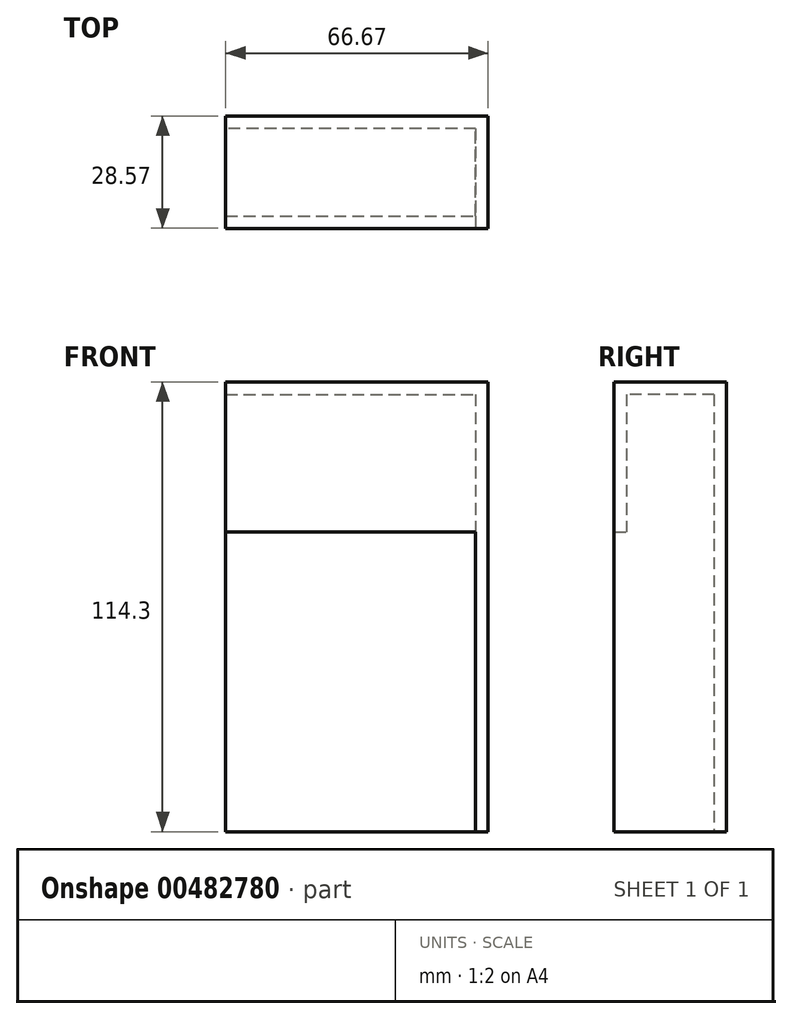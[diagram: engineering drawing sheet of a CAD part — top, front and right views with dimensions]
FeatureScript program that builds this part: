
annotation { "Feature Type Name" : "Feature", "Feature Type Description" : "" }
export const myFeature = defineFeature(function(context is Context, id is Id, definition is map)
    precondition{}
    {
        {
            var Q0;
            Q0=qCreatedBy(makeId("Front.planeOp"),FACE);
            var sketch = newSketch(context, id + "F0", { "sketchPlane" : qUnion([Q0])});
            skLineSegment(sketch, "E0.bottom", {"start": v(-31.75, 19.05) * mm, "end": v(31.75, 19.05) * mm});
            skLineSegment(sketch, "E0.top", {"start": v(-31.75, -19.05) * mm, "end": v(31.75, -19.05) * mm});
            skLineSegment(sketch, "E0.left", {"start": v(-31.75, 19.05) * mm, "end": v(-31.75, -19.05) * mm});
            skLineSegment(sketch, "E0.right", {"start": v(31.75, 19.05) * mm, "end": v(31.75, -19.05) * mm});
            skPoint(sketch, "E1", {"position": v(0, 0) * mm});
            skPoint(sketch, "E1.positionSnap0", {"position": v(-31.75, 0) * mm});
            skPoint(sketch, "E1.positionSnap1", {"position": v(0, 19.05) * mm});
            skSolve(sketch);
        }
        {
            var Q0;
            Q0=makeQuery(id+"F0.imprint","IMPRINT",FACE,{"disambiguationData":[TD([[makeQuery(id+"F0.imprint","IMPRINT",EDGE,{"derivedFrom":sQuery(id+"F0.wireOp",EDGE,"E0.bottom")}),-1.0]])]});
            extrude(context, id + "F1", {"entities" : qUnion([Q0]), "depth" : 3.17 * mm});
        }
        {
            var Q0;
            Q0=makeQuery(id+"F1.opExtrude","SWEPT_FACE",FACE,{"disambiguationData":[OSD([sQuery(id+"F0.wireOp",EDGE,"E0.right")])]});
            var sketch = newSketch(context, id + "F2", { "sketchPlane" : qUnion([Q0])});
            skLineSegment(sketch, "E2.bottom", {"start": v(-3.18, 19.05) * mm, "end": v(22.23, 19.05) * mm});
            skLineSegment(sketch, "E2.top", {"start": v(-3.18, -19.05) * mm, "end": v(22.23, -19.05) * mm});
            skLineSegment(sketch, "E2.left", {"start": v(-3.18, 19.05) * mm, "end": v(-3.18, -19.05) * mm});
            skLineSegment(sketch, "E2.right", {"start": v(22.23, 19.05) * mm, "end": v(22.23, -19.05) * mm});
            skSolve(sketch);
        }
        {
            var Q0;
            {var subQ2=sQuery(id+"F2.wireOp",EDGE,"E2.right");Q0=makeQuery(id+"F2.imprint","IMPRINT",FACE,{"disambiguationData":[TD([[makeQuery(id+"F2.imprint","IMPRINT",EDGE,{"derivedFrom":subQ2}),-1.0]])]});}
            var Q1;
            {var subQ2=sQuery(id+"F2.wireOp",EDGE,"E2.left");Q1=makeQuery(id+"F2.imprint","IMPRINT",FACE,{"disambiguationData":[TD([[makeQuery(id+"F2.imprint","IMPRINT",EDGE,{"derivedFrom":subQ2}),1.0]])]});}
            extrude(context, id + "F3", {"entities" : qUnion([Q0, Q1]), "operationType" : NewBodyOperationType.ADD, "depth" : 3.17 * mm});
        }
        {
            var Q0;
            Q0=makeQuery(id+"F3.boolean.opBoolean","MERGE",FACE,{"derivedFrom":[makeQuery(id+"F1.opExtrude","SWEPT_FACE",FACE,{"disambiguationData":[OSD([sQuery(id+"F0.wireOp",EDGE,"E0.top")])]}),makeQuery(id+"F3.opExtrude","SWEPT_FACE",FACE,{"disambiguationData":[OSD([sQuery(id+"F2.wireOp",EDGE,"E2.top")])]})]});
            var sketch = newSketch(context, id + "F4", { "sketchPlane" : qUnion([Q0])});
            skLineSegment(sketch, "E3.bottom", {"start": v(34.92, -22.23) * mm, "end": v(31.75, -22.23) * mm});
            skLineSegment(sketch, "E3.top", {"start": v(34.92, 3.18) * mm, "end": v(31.75, 3.18) * mm});
            skLineSegment(sketch, "E3.left", {"start": v(34.92, -22.23) * mm, "end": v(34.92, 3.18) * mm});
            skLineSegment(sketch, "E3.right", {"start": v(31.75, -22.23) * mm, "end": v(31.75, 3.18) * mm});
            skSolve(sketch);
        }
        {
            var Q0;
            {var subQ1=sQuery(id+"F4.wireOp",EDGE,"E3.bottom");Q0=makeQuery(id+"F4.imprint","IMPRINT",FACE,{"disambiguationData":[TD([[makeQuery(id+"F4.imprint","IMPRINT",EDGE,{"derivedFrom":subQ1}),-1.0]])]});}
            extrude(context, id + "F5", {"entities" : qUnion([Q0]), "operationType" : NewBodyOperationType.ADD, "depth" : 76.2 * mm});
        }
        {
            var Q0;
            Q0=makeQuery(id+"F5.boolean.opBoolean","MERGE",FACE,{"derivedFrom":[makeQuery(id+"F3.opExtrude","SWEPT_FACE",FACE,{"disambiguationData":[OSD([sQuery(id+"F2.wireOp",EDGE,"E2.right")])]}),makeQuery(id+"F5.opExtrude","SWEPT_FACE",FACE,{"disambiguationData":[OSD([sQuery(id+"F4.wireOp",EDGE,"E3.bottom")])]})]});
            var sketch = newSketch(context, id + "F6", { "sketchPlane" : qUnion([Q0])});
            skLineSegment(sketch, "E4.bottom", {"start": v(-31.75, 19.05) * mm, "end": v(31.75, 19.05) * mm});
            skLineSegment(sketch, "E4.top", {"start": v(-31.75, -95.25) * mm, "end": v(31.75, -95.25) * mm});
            skLineSegment(sketch, "E4.left", {"start": v(-31.75, 19.05) * mm, "end": v(-31.75, -95.25) * mm});
            skLineSegment(sketch, "E4.right", {"start": v(31.75, 19.05) * mm, "end": v(31.75, -95.25) * mm});
            skLineSegment(sketch, "E5.bottom", {"start": v(-34.92, 19.05) * mm, "end": v(-31.75, 19.05) * mm});
            skLineSegment(sketch, "E5.top", {"start": v(-34.92, -95.25) * mm, "end": v(-31.75, -95.25) * mm});
            skLineSegment(sketch, "E5.left", {"start": v(-34.92, 19.05) * mm, "end": v(-34.92, -95.25) * mm});
            skSolve(sketch);
        }
        {
            var Q0;
            Q0=makeQuery(id+"F6.imprint","IMPRINT",FACE,{"disambiguationData":[TD([[makeQuery(id+"F6.imprint","IMPRINT",EDGE,{"derivedFrom":sQuery(id+"F6.wireOp",EDGE,"E4.bottom")}),-1.0]])]});
            var Q1;
            Q1=makeQuery(id+"F6.imprint","IMPRINT",FACE,{"disambiguationData":[TD([[makeQuery(id+"F6.imprint","IMPRINT",EDGE,{"derivedFrom":sQuery(id+"F6.wireOp",EDGE,"E5.bottom")}),-1.0]])]});
            extrude(context, id + "F7", {"entities" : qUnion([Q0, Q1]), "operationType" : NewBodyOperationType.ADD, "depth" : 3.17 * mm});
        }
        {
            var Q0;
            Q0=makeQuery(id+"F7.boolean.opBoolean","MERGE",FACE,{"derivedFrom":[makeQuery(id+"F3.boolean.opBoolean","MERGE",FACE,{"derivedFrom":[makeQuery(id+"F1.opExtrude","SWEPT_FACE",FACE,{"disambiguationData":[OSD([sQuery(id+"F0.wireOp",EDGE,"E0.bottom")])]}),makeQuery(id+"F3.opExtrude","SWEPT_FACE",FACE,{"disambiguationData":[OSD([sQuery(id+"F2.wireOp",EDGE,"E2.bottom")])]})]}),makeQuery(id+"F7.opExtrude","SWEPT_FACE",FACE,{"disambiguationData":[OSD([sQuery(id+"F6.wireOp",EDGE,"E4.bottom"),sQuery(id+"F6.wireOp",EDGE,"E5.bottom")])]})]});
            var sketch = newSketch(context, id + "F8", { "sketchPlane" : qUnion([Q0])});
            skLineSegment(sketch, "E6.bottom", {"start": v(-31.75, 25.4) * mm, "end": v(34.92, 25.4) * mm});
            skLineSegment(sketch, "E6.top", {"start": v(-31.75, -3.18) * mm, "end": v(34.92, -3.18) * mm});
            skLineSegment(sketch, "E6.left", {"start": v(-31.75, 25.4) * mm, "end": v(-31.75, -3.18) * mm});
            skLineSegment(sketch, "E6.right", {"start": v(34.92, 25.4) * mm, "end": v(34.92, -3.18) * mm});
            skLineSegment(sketch, "E7.bottom", {"start": v(-31.75, 22.23) * mm, "end": v(31.75, 22.23) * mm});
            skLineSegment(sketch, "E7.top", {"start": v(-31.75, 0) * mm, "end": v(31.75, 0) * mm});
            skLineSegment(sketch, "E7.left", {"start": v(-31.75, 22.23) * mm, "end": v(-31.75, 0) * mm});
            skLineSegment(sketch, "E7.right", {"start": v(31.75, 22.23) * mm, "end": v(31.75, 0) * mm});
            skSolve(sketch);
        }
        {
            var Q0;
            Q0=makeQuery(id+"F8.imprint","IMPRINT",FACE,{"disambiguationData":[TD([[makeQuery(id+"F8.imprint","IMPRINT",EDGE,{"derivedFrom":sQuery(id+"F8.wireOp",EDGE,"E7.bottom")}),1.0]])]});
            extrude(context, id + "F9", {"entities" : qUnion([Q0]), "operationType" : NewBodyOperationType.ADD, "oppositeDirection" : true, "depth" : 3.17 * mm});
        }
    });
